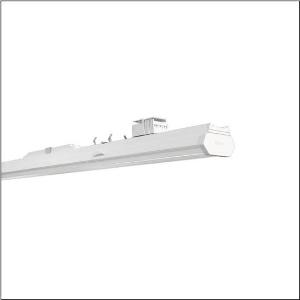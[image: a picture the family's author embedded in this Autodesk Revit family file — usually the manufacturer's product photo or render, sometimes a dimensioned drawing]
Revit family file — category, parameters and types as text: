
# Revit family: licross_r__21_protected_mo_52td12cn675f_4ad1
name_source: partatom
category: Lighting Fixtures
units: mm (PartAtom-declared; Revit-internal decimal feet)

## family parameters
Cut with Voids When Loaded = No
Host = Face
Light Source = No
Part Type = Normal
Room Calculation Point = No
Round Connector Dimension = Use Diameter
Shared = No

## types (1)
- --- (1 x LED, 7960 lm, 48.5 W, 6500K)
    Apparent Load = 49 VA
    CIE Flux Codes = 73 92 98 99 100
    Color Rendering = 80
    Color Temperature = 6500K
    Default Elevation = 1800 mm
    Description = Licross® 21 Protected MO, luminaire insert, of sheet steel, galvanised, coil coated, white, length: 1.500mm, width: 90mm, height: 101mm, LED rated luminous flux: 7.940lm, light colour: 865, control gear: ON/OFF Multilumen, CLOi, control gear: ECG Multilumen, with plug, 3-pole, with phase selection, mains connection: 220..240V, AC, 50/60Hz, start of lifetime: 49W, end of service life: 55W, halogen-free wiring, primary optical cover: cover, of PMMA, light emission: direct distribution, primary light characteristic: symmetric, protection rating (complete): IP54, insulation class (complete): insulation class I (protective earthing), certification: CE, ENEC, VDE, UKCA, protection symbol: D if used in an environment with non-conductive dust loads with corresponding accessories, impact resistance: IK06, permissible ambient temperature for indoor applications: -35..+45°C, corresponds to IFS (International Featured Standards) requirements for safety and quality in the food industry, reducing of maximum allowable ambient temperature of 5°C with ceiling mounting, LABS conformity tested according to VDMA 24364:2018-05, packaging unit: 1 piece
    Height = 92 mm
    Lamp = 1 x LED
    Lamp Light Flux = 7960 lm
    Lamp Power = 48.5 W
    Lamp count = 1
    Length = 1500 mm
    Luminous efficacy = 164 lm/W
    Manufacturer = Siteco
    ModVariant = No
    Model = 52TD12CN675F
    Mounting Place = Ceiling
    Mounting Type = Pendant
    Number of Poles = 1
    OnlyDefault = Yes
    Power Factor = 1
    Product Name = Licross® 21 Protected MO
    Product group = luminaire insert
    ProductGroupID = 901
    Protection Class = Protection class I
    Protection Degree = IP 54
    RLX_Detail_Level = 1
    RLX_Emergency_Light_Flux = 0 lm
    RLX_Emergency_Type = 0
    RLX_Emergency_Type_DB = No
    RlxData = <blob elided: 22053 chars, md5=cce0cc37>
    Socket = socket
    Standby Power = 0 W
    System Light Flux = 7960 lm
    System Power = 49 W
    Type Comments = factory setting: luminous flux: 100 % | (A | C | E) | 117 mA
    Type Image = l_1256148.jpg
    URL = http://relux.com
    VarID = @adj_131629
    Voltage = 0 V
    Weight = 0.00 kg
    Width = 88 mm

## geometry (parser evidence)
native form markers: Blend x4, Sweep x11
no freeform markers — native parametric forms only
